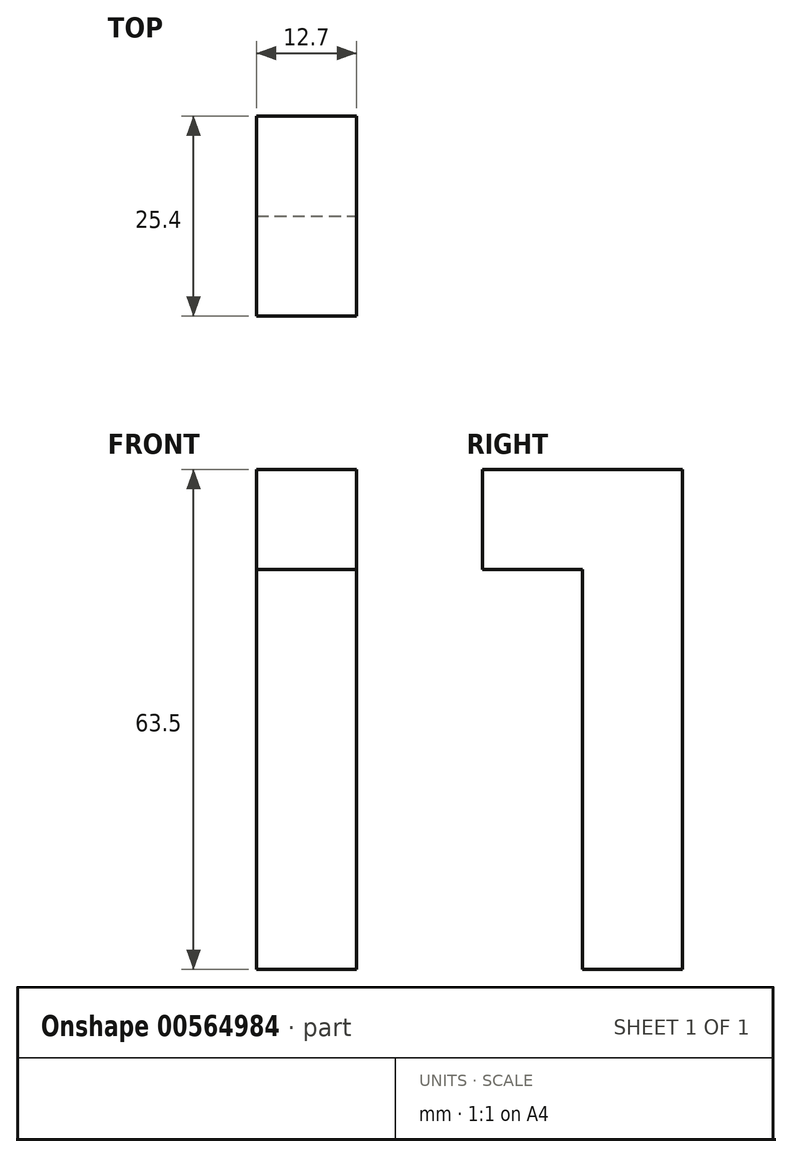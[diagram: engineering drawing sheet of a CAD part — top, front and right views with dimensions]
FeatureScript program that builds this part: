
annotation { "Feature Type Name" : "Feature", "Feature Type Description" : "" }
export const myFeature = defineFeature(function(context is Context, id is Id, definition is map)
    precondition{}
    {
        {
            var Q0;
            Q0=qCreatedBy(makeId("Top.planeOp"),FACE);
            var sketch = newSketch(context, id + "F0", { "sketchPlane" : qUnion([Q0])});
            skLineSegment(sketch, "E0.bottom", {"start": v(-34.09, 36.8) * mm, "end": v(-21.39, 36.8) * mm});
            skLineSegment(sketch, "E0.top", {"start": v(-34.09, 24.1) * mm, "end": v(-21.39, 24.1) * mm});
            skLineSegment(sketch, "E0.left", {"start": v(-34.09, 36.8) * mm, "end": v(-34.09, 24.1) * mm});
            skLineSegment(sketch, "E0.right", {"start": v(-21.39, 36.8) * mm, "end": v(-21.39, 24.1) * mm});
            skSolve(sketch);
        }
        {
            var Q0;
            Q0=makeQuery(id+"F0.imprint","IMPRINT",FACE,{"disambiguationData":[TD([[makeQuery(id+"F0.imprint","IMPRINT",EDGE,{"derivedFrom":sQuery(id+"F0.wireOp",EDGE,"E0.bottom")}),-1.0]])]});
            extrude(context, id + "F1", {"entities" : qUnion([Q0]), "depth" : 63.5 * mm, "offsetDistance" : 25.4 * mm});
        }
        {
            var Q0;
            Q0=makeQuery(id+"F1.opExtrude","SWEPT_FACE",FACE,{"disambiguationData":[OSD([sQuery(id+"F0.wireOp",EDGE,"E0.top")])]});
            var sketch = newSketch(context, id + "F2", { "sketchPlane" : qUnion([Q0])});
            skLineSegment(sketch, "E1.bottom", {"start": v(-34.09, 63.5) * mm, "end": v(-21.39, 63.5) * mm});
            skLineSegment(sketch, "E1.top", {"start": v(-34.09, 50.8) * mm, "end": v(-21.39, 50.8) * mm});
            skLineSegment(sketch, "E1.left", {"start": v(-34.09, 63.5) * mm, "end": v(-34.09, 50.8) * mm});
            skLineSegment(sketch, "E1.right", {"start": v(-21.39, 63.5) * mm, "end": v(-21.39, 50.8) * mm});
            skSolve(sketch);
        }
        {
            var Q0;
            Q0=makeQuery(id+"F2.imprint","IMPRINT",FACE,{"disambiguationData":[TD([[makeQuery(id+"F2.imprint","IMPRINT",EDGE,{"derivedFrom":sQuery(id+"F2.wireOp",EDGE,"E1.bottom")}),-1.0]])]});
            extrude(context, id + "F3", {"entities" : qUnion([Q0]), "operationType" : NewBodyOperationType.ADD, "depth" : 12.7 * mm, "offsetDistance" : 25.4 * mm});
        }
    });
